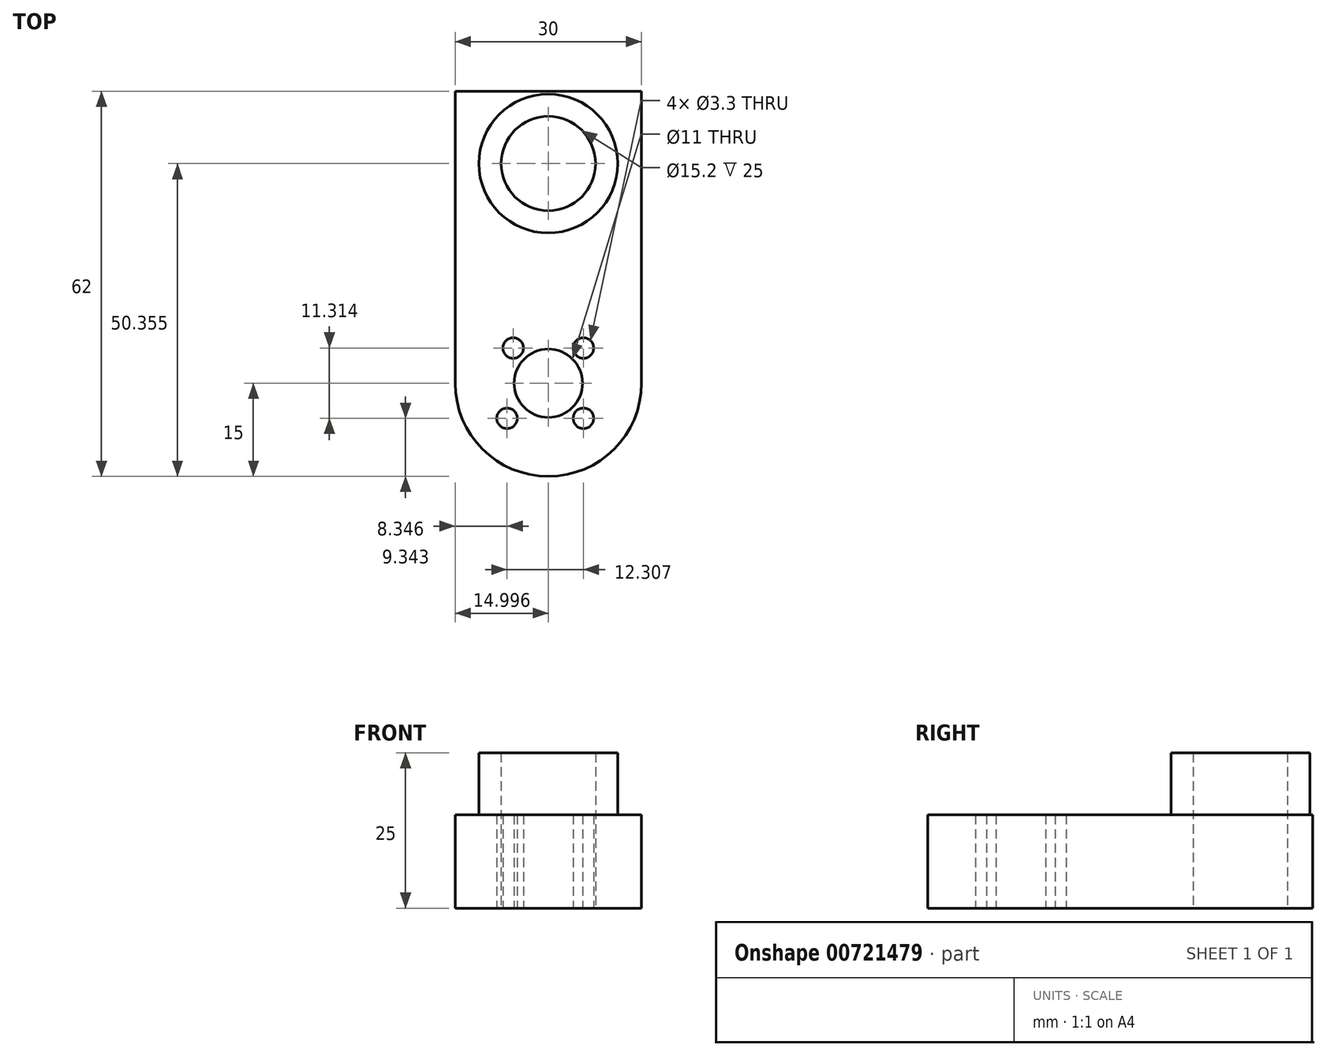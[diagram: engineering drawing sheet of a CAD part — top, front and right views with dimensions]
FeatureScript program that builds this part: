
annotation { "Feature Type Name" : "Feature", "Feature Type Description" : "" }
export const myFeature = defineFeature(function(context is Context, id is Id, definition is map)
    precondition{}
    {
        {
            var Q0;
            Q0=qCreatedBy(makeId("Top.planeOp"),FACE);
            var sketch = newSketch(context, id + "F0", { "sketchPlane" : qUnion([Q0])});
            skPoint(sketch, "E0.start.orphan", {"position": v(-34.23, 53.78) * mm});
            skPoint(sketch, "E1.trimOffspring.end.orphan", {"position": v(-34.23, 5.76) * mm});
            skPoint(sketch, "E2.endSnap0", {"position": v(-54.23, 38.78) * mm});
            skCircle(sketch, "E3", {"center": v(-39.9, 14.08) * mm, "radius": 1.65 * mm});
            skCircle(sketch, "E4", {"center": v(-40.88, 2.76) * mm, "radius": 1.65 * mm});
            skCircle(sketch, "E5", {"center": v(-28.58, 2.76) * mm, "radius": 1.65 * mm});
            skCircle(sketch, "E6", {"center": v(-28.58, 14.08) * mm, "radius": 1.65 * mm});
            skCircle(sketch, "E7", {"center": v(-34.23, 8.42) * mm, "radius": 5.5 * mm});
            skPoint(sketch, "E8.orphan", {"position": v(-34.23, -3.58) * mm});
            skLineSegment(sketch, "E9", {"start": v(-19.23, 53.78) * mm, "end": v(-19.23, 8.42) * mm});
            skLineSegment(sketch, "E10", {"start": v(-49.23, 55.42) * mm, "end": v(-49.23, 8.42) * mm});
            skArc(sketch, "E11", {"start": v(-49.23, 8.42) * mm, "mid": v(-34.23, -6.58) * mm, "end": v(-19.23, 8.42) * mm});
            skCircle(sketch, "E12", {"center": v(-34.23, 43.78) * mm, "radius": 7.6 * mm});
            skCircle(sketch, "E13", {"center": v(-34.23, 43.78) * mm, "radius": 11.18 * mm});
            skLineSegment(sketch, "E14", {"start": v(-49.23, 55.42) * mm, "end": v(-19.23, 55.42) * mm});
            skLineSegment(sketch, "E15", {"start": v(-19.23, 55.42) * mm, "end": v(-19.23, 53.78) * mm});
            skSolve(sketch);
        }
        {
            var Q0;
            Q0=makeQuery(id+"F0.imprint","IMPRINT",FACE,{"disambiguationData":[TD([[makeQuery(id+"F0.imprint","IMPRINT",EDGE,{"derivedFrom":sQuery(id+"F0.wireOp",EDGE,"E3")}),-1.0]])]});
            extrude(context, id + "F1", {"entities" : qUnion([Q0]), "depth" : 15 * mm, "offsetDistance" : 25 * mm});
        }
        {
            var Q0;
            Q0=qSketchRegion(id+"FbwitGv9QD3be2T_1",true);
            var Q1;
            Q1=makeQuery(id+"F0.imprint","IMPRINT",FACE,{"disambiguationData":[TD([[makeQuery(id+"F0.imprint","IMPRINT",EDGE,{"derivedFrom":sQuery(id+"F0.wireOp",EDGE,"E12")}),-1.0]])]});
            extrude(context, id + "F2", {"entities" : qUnion([Q0, Q1]), "operationType" : NewBodyOperationType.ADD, "depth" : 25 * mm, "offsetDistance" : 25 * mm});
        }
    });
